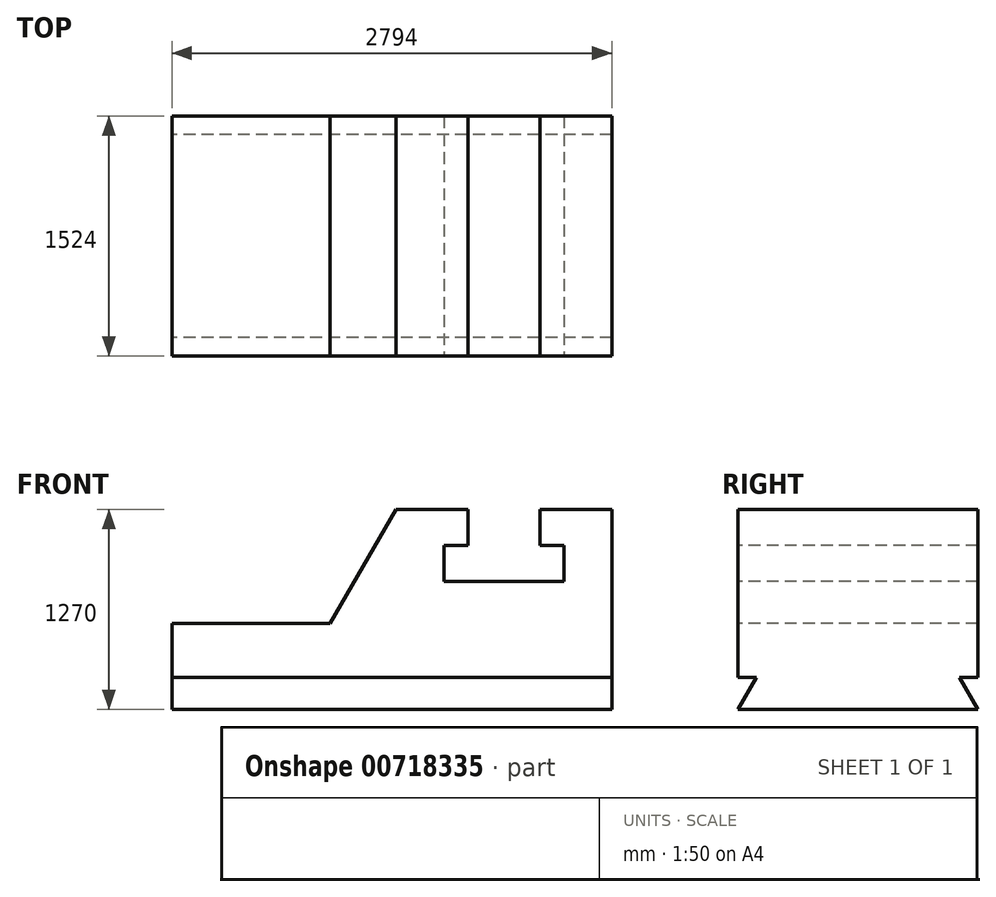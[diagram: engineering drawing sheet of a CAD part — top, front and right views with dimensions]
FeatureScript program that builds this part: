
annotation { "Feature Type Name" : "Feature", "Feature Type Description" : "" }
export const myFeature = defineFeature(function(context is Context, id is Id, definition is map)
    precondition{}
    {
        {
            var Q0;
            Q0=qCreatedBy(makeId("Top.planeOp"),FACE);
            var sketch = newSketch(context, id + "F0", { "sketchPlane" : qUnion([Q0])});
            skLineSegment(sketch, "E0", {"start": v(2677.8, 27.2) * mm, "end": v(-116.2, 27.2) * mm});
            skLineSegment(sketch, "E1", {"start": v(2677.8, 27.2) * mm, "end": v(2677.8, -1496.8) * mm});
            skLineSegment(sketch, "E2", {"start": v(2677.8, -1496.8) * mm, "end": v(-116.2, -1496.8) * mm});
            skLineSegment(sketch, "E3", {"start": v(-116.2, -1496.8) * mm, "end": v(-116.2, 27.2) * mm});
            skLineSegment(sketch, "E4", {"start": v(2677.8, 27.2) * mm, "end": v(2220.6, 27.2) * mm});
            skLineSegment(sketch, "E5", {"start": v(2220.6, 27.2) * mm, "end": v(2220.6, -1496.8) * mm});
            skLineSegment(sketch, "E6", {"start": v(2220.6, -1496.8) * mm, "end": v(1763.4, -1496.8) * mm});
            skLineSegment(sketch, "E7", {"start": v(1763.4, -1496.8) * mm, "end": v(1763.4, 27.2) * mm});
            skLineSegment(sketch, "E8", {"start": v(1763.4, 27.2) * mm, "end": v(1306.2, 27.2) * mm});
            skLineSegment(sketch, "E9", {"start": v(1306.2, 27.2) * mm, "end": v(1306.2, -1496.8) * mm});
            skSolve(sketch);
        }
        {
            var Q0;
            Q0=qSketchRegion(id+"F0",true);
            extrude(context, id + "F1", {"entities" : qUnion([Q0]), "oppositeDirection" : true, "depth" : 1270 * mm, "offsetDistance" : 25.4 * mm});
        }
        {
            var Q0;
            Q0=makeQuery(id+"F1.opExtrude","SWEPT_FACE",FACE,{"disambiguationData":[OSD([sQuery(id+"F0.wireOp",EDGE,"E2"),sQuery(id+"F0.wireOp",EDGE,"E6")])]});
            var sketch = newSketch(context, id + "F2", { "sketchPlane" : qUnion([Q0])});
            skLineSegment(sketch, "E10", {"start": v(2677.8, 0) * mm, "end": v(2220.6, 0) * mm});
            skLineSegment(sketch, "E11", {"start": v(2220.6, 0) * mm, "end": v(1763.4, 0) * mm});
            skLineSegment(sketch, "E12", {"start": v(1763.4, 0) * mm, "end": v(1763.4, -228.6) * mm});
            skLineSegment(sketch, "E13", {"start": v(2220.6, 0) * mm, "end": v(2220.6, -228.6) * mm});
            skLineSegment(sketch, "E14", {"start": v(2220.6, -228.6) * mm, "end": v(2373, -228.6) * mm});
            skLineSegment(sketch, "E15", {"start": v(2373, -228.6) * mm, "end": v(2373, -457.2) * mm});
            skLineSegment(sketch, "E16", {"start": v(2373, -457.2) * mm, "end": v(1611, -457.2) * mm});
            skLineSegment(sketch, "E17", {"start": v(1611, -457.2) * mm, "end": v(1611, -228.6) * mm});
            skLineSegment(sketch, "E18", {"start": v(1611, -228.6) * mm, "end": v(1763.4, -228.6) * mm});
            skSolve(sketch);
        }
        {
            var Q0;
            Q0=makeQuery(id+"F2.imprint","IMPRINT",FACE,{"disambiguationData":[TD([[makeQuery(id+"F2.imprint","IMPRINT",EDGE,{"derivedFrom":sQuery(id+"F2.wireOp",EDGE,"E11")}),1.0]])]});
            extrude(context, id + "F3", {"entities" : qUnion([Q0]), "operationType" : NewBodyOperationType.REMOVE, "endBound" : BoundingType.THROUGH_ALL, "oppositeDirection" : true, "depth" : 25.4 * mm, "offsetDistance" : 25.4 * mm});
        }
        {
            var Q0;
            Q0=makeQuery(id+"F1.opExtrude","SWEPT_FACE",FACE,{"disambiguationData":[OSD([sQuery(id+"F0.wireOp",EDGE,"E3")])]});
            var sketch = newSketch(context, id + "F4", { "sketchPlane" : qUnion([Q0])});
            skLineSegment(sketch, "E19", {"start": v(1496.8, -1270) * mm, "end": v(601.76, 280.25) * mm});
            skLineSegment(sketch, "E20", {"start": v(-27.2, -1270) * mm, "end": v(867.83, 280.25) * mm});
            skLineSegment(sketch, "E21", {"start": v(-27.2, -1270) * mm, "end": v(-27.2, -1066.8) * mm});
            skLineSegment(sketch, "E22", {"start": v(-27.2, -1066.8) * mm, "end": v(1496.8, -1066.8) * mm});
            skLineSegment(sketch, "E23", {"start": v(1496.8, -1066.8) * mm, "end": v(1496.8, -1270) * mm});
            skSolve(sketch);
        }
        {
            var Q0;
            {var subQ0=sQuery(id+"F4.wireOp",EDGE,"E21");Q0=makeQuery(id+"F4.imprint","IMPRINT",FACE,{"disambiguationData":[TD([[makeQuery(id+"F4.imprint","IMPRINT",EDGE,{"derivedFrom":subQ0}),-1.0]])]});}
            extrude(context, id + "F5", {"entities" : qUnion([Q0]), "operationType" : NewBodyOperationType.REMOVE, "endBound" : BoundingType.THROUGH_ALL, "oppositeDirection" : true, "depth" : 25.4 * mm, "offsetDistance" : 25.4 * mm});
        }
        {
            var Q0;
            {var subQ0=sQuery(id+"F4.wireOp",EDGE,"E23");Q0=makeQuery(id+"F4.imprint","IMPRINT",FACE,{"disambiguationData":[TD([[makeQuery(id+"F4.imprint","IMPRINT",EDGE,{"derivedFrom":subQ0}),1.0]])]});}
            extrude(context, id + "F6", {"entities" : qUnion([Q0]), "operationType" : NewBodyOperationType.REMOVE, "endBound" : BoundingType.THROUGH_ALL, "oppositeDirection" : true, "depth" : 25.4 * mm, "offsetDistance" : 25.4 * mm});
        }
        {
            var Q0;
            Q0=makeQuery(id+"F1.opExtrude","SWEPT_FACE",FACE,{"disambiguationData":[OSD([sQuery(id+"F0.wireOp",EDGE,"E2"),sQuery(id+"F0.wireOp",EDGE,"E6")])]});
            var sketch = newSketch(context, id + "F7", { "sketchPlane" : qUnion([Q0])});
            skLineSegment(sketch, "E24", {"start": v(1763.4, 0) * mm, "end": v(1306.2, 0) * mm});
            skLineSegment(sketch, "E25", {"start": v(1306.2, 0) * mm, "end": v(888.16, -724.07) * mm});
            skLineSegment(sketch, "E26", {"start": v(888.16, -724.07) * mm, "end": v(-116.2, -724.07) * mm});
            skSolve(sketch);
        }
        {
            var Q0;
            {var subQ0=sQuery(id+"F7.wireOp",EDGE,"E25");Q0=makeQuery(id+"F7.imprint","IMPRINT",FACE,{"disambiguationData":[TD([[makeQuery(id+"F7.imprint","IMPRINT",EDGE,{"derivedFrom":subQ0}),-1.0]])]});}
            extrude(context, id + "F8", {"entities" : qUnion([Q0]), "operationType" : NewBodyOperationType.REMOVE, "endBound" : BoundingType.THROUGH_ALL, "oppositeDirection" : true, "depth" : 25.4 * mm, "offsetDistance" : 25.4 * mm});
        }
    });
